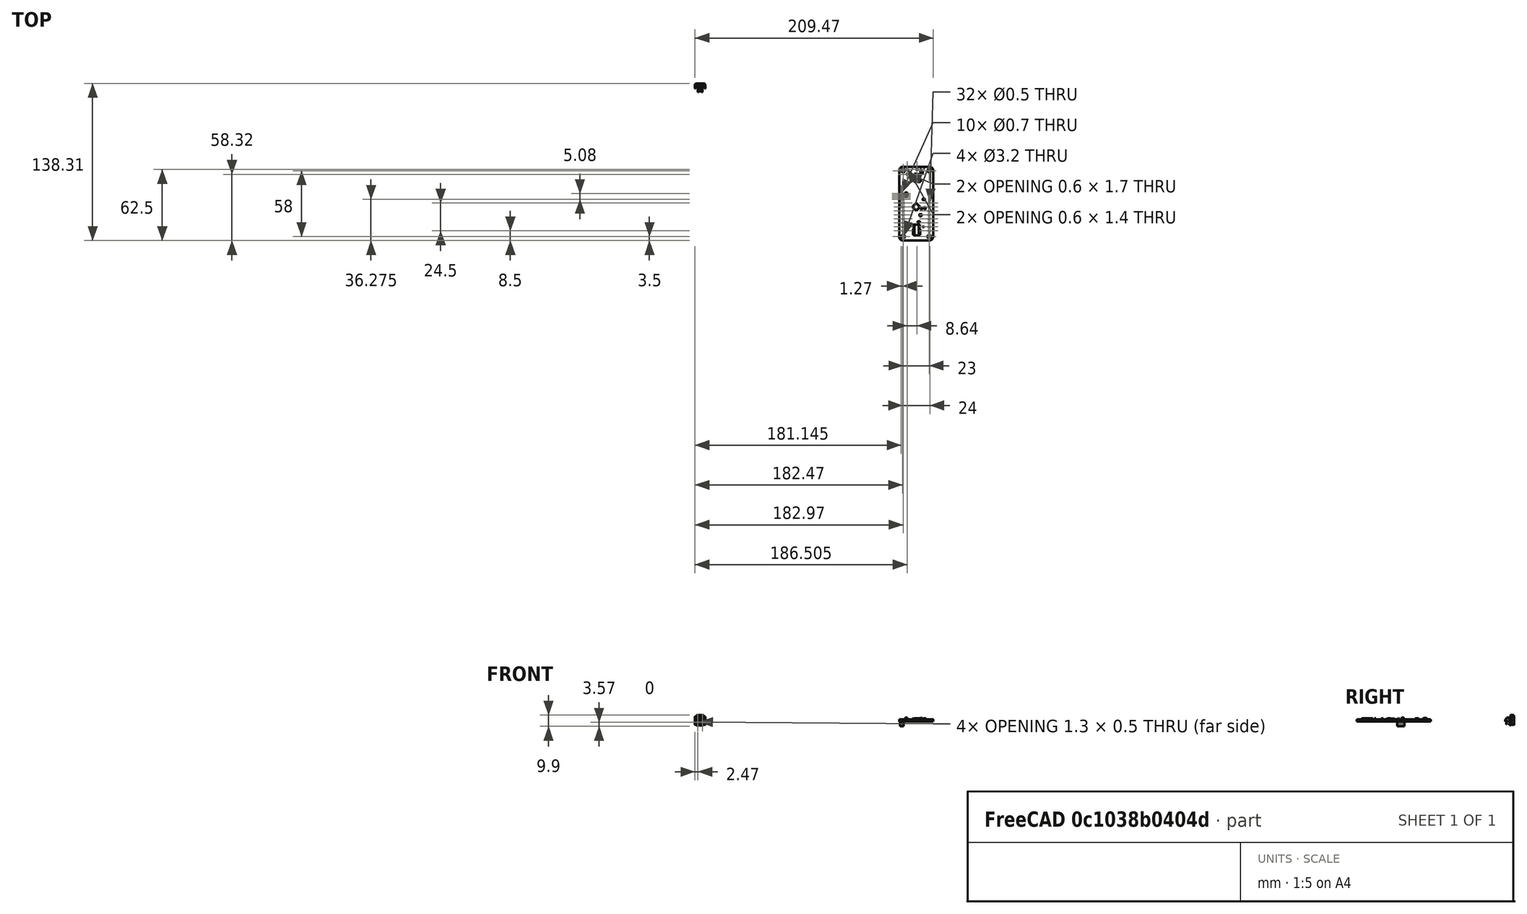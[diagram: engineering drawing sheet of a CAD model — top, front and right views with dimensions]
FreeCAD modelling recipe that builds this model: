
FCSTD DOCUMENT  (FreeCAD 0.21R33771 (Git))
Label: fc_r3
License: All rights reserved
LicenseURL: http://en.wikipedia.org/wiki/All_rights_reserved
objects: Part::Feature×103, App::Link×54, App::Part×14, PartDesign::CoordinateSystem×1, Sketcher::SketchObject×1
note: 105 computed .brp shape members not serialized (recipe doc carries the construction recipe); baked Part::Feature solids carry a one-line shape summary decoded from their .brp

FEATURE [PartDesign::CoordinateSystem] Local_CS_fc8e
  AttacherType = Attacher::AttachEngine3D
  MapMode = 2
  Support = -> [X_Axis001]
FEATURE [Part::Feature] Pcb_fc8e
  shape: bbox 30 x 65 x 1.6 mm, 85 faces (baked)
FEATURE [Sketcher::SketchObject] PCB_Sketch_fc8e
  FullyConstrained = false
  sketch-geometry (9):
    g0: LineSegment StartX=205 StartY=-73.5 StartZ=0 EndX=205 EndY=-131.5 EndZ=0
    g1: LineSegment StartX=178.5 StartY=-135 StartZ=0 EndX=201.5 EndY=-135 EndZ=0
    g2: LineSegment StartX=175 StartY=-73.5 StartZ=0 EndX=175 EndY=-131.5 EndZ=0
    g3: LineSegment StartX=178.5 StartY=-70 StartZ=0 EndX=197 EndY=-70 EndZ=0
    g4: LineSegment StartX=197 StartY=-70 StartZ=0 EndX=201.5 EndY=-70 EndZ=0
    g5: ArcOfCircle CenterX=178.5 CenterY=-131.5 CenterZ=0 NormalX=0 NormalY=0 NormalZ=-1 AngleXU=-1.5708 Radius=3.5 StartAngle=0 EndAngle=1.5708
    g6: ArcOfCircle CenterX=201.5 CenterY=-131.5 CenterZ=0 NormalX=0 NormalY=0 NormalZ=-1 AngleXU=3.14159 Radius=3.5 StartAngle=0 EndAngle=1.5708
    g7: ArcOfCircle CenterX=178.5 CenterY=-73.5 CenterZ=0 NormalX=0 NormalY=0 NormalZ=-1 AngleXU=-2.59331e-07 Radius=3.5 StartAngle=0 EndAngle=1.5708
    g8: ArcOfCircle CenterX=201.5 CenterY=-73.5 CenterZ=0 NormalX=0 NormalY=0 NormalZ=-1 AngleXU=1.5708 Radius=3.5 StartAngle=0 EndAngle=1.5708
  constraints (9):
    c: Coincident(g2,g5)
    c: Coincident(g2,g7)
    c: Coincident(g1,g5)
    c: Coincident(g3,g7)
    c: Coincident(g3,g4)
    c: Coincident(g1,g6)
    c: Coincident(g4,g8)
    c: Coincident(g0,g6)
    c: Coincident(g0,g8)
FEATURE [App::Part] Board_Geoms_fc8e
  Group = -> [Pcb_fc8e,PCB_Sketch_fc8e]
  Origin = -> Origin
FEATURE [Part::Feature] Part__Feature  label="SOLID"
  shape: bbox 4.25 x 5.5 x 5.806 mm, 112 faces (baked)
FEATURE [App::Part] _30480210  label="J15_530480210_eba29879c98""
  Group = -> [Part__Feature]
  Origin = -> Origin008
  Placement = pos=(178.75,-116,3) rot=(1,0,0;1.5708rad)
FEATURE [Part::Feature] Shape  label="AP2112K-3.3V2_SOT_23_5_dac772f8d32""
  Placement = pos=(194.5,-75,0) rot=(0,0,1;3.14159rad)
  shape: bbox 2.8 x 2.9 x 1.55 mm, 109 faces (baked)
FEATURE [Part::Feature] Shape001  label="R31_R_0402_1005Metric_05aedb9767e""
  Placement = pos=(196.225,-123.071,0) rot=(0,0,1;3.14159rad)
  shape: bbox 1 x 0.5 x 0.35 mm, 26 faces (baked)
FEATURE [App::Link] J15_530480210_eba29879c98__ln_  label="J12_530480210_0c2ba19a673""
  LinkPlacement = pos=(178.75,-105.5,3) rot=(1,0,0;1.5708rad)
  LinkedObject = -> _30480210
  Placement = pos=(178.75,-105.5,3) rot=(1,0,0;1.5708rad)
FEATURE [App::Link] J15_530480210_eba29879c98__ln_001  label="J23_530480210_43af08e91fe""
  LinkPlacement = pos=(201.25,-112.5,3) rot=(0,0.707107,0.707107;3.14159rad)
  LinkedObject = -> _30480210
  Placement = pos=(201.25,-112.5,3) rot=(0,0.707107,0.707107;3.14159rad)
FEATURE [App::Link] R31_R_0402_1005Metric_05aedb9767e__ln_  label="R3_R_0402_1005Metric_8d72cd1c525""
  LinkPlacement = pos=(196.4,-111.45,0) rot=(0,0,1;3.14159rad)
  LinkedObject = -> Shape001
  Placement = pos=(196.4,-111.45,0) rot=(0,0,1;3.14159rad)
FEATURE [App::Link] R31_R_0402_1005Metric_05aedb9767e__ln_001  label="R25_R_0402_1005Metric_978085bccb1""
  LinkPlacement = pos=(196.128,-132.5,0) rot=(0,0,1;3.14159rad)
  LinkedObject = -> Shape001
  Placement = pos=(196.128,-132.5,0) rot=(0,0,1;3.14159rad)
FEATURE [Part::Feature] Shape002  label="R17_R_0805_2012Metric_b5a45a613a7""
  Placement = pos=(196.6,-98.8,0) rot=(0,0,1;0rad)
  shape: bbox 2 x 1.2 x 0.45 mm, 26 faces (baked)
FEATURE [App::Link] J15_530480210_eba29879c98__ln_002  label="J14_530480210_c20acc79bf5""
  LinkPlacement = pos=(178.75,-112.5,3) rot=(1,0,0;1.5708rad)
  LinkedObject = -> _30480210
  Placement = pos=(178.75,-112.5,3) rot=(1,0,0;1.5708rad)
FEATURE [Part::Feature] Shape003  label="C7_C_0805_2012Metric_171301cf5fe""
  Placement = pos=(197.6,-106.6,0) rot=(0,0,1;1.5708rad)
  shape: bbox 1.25 x 2 x 1.25 mm, 28 faces (baked)
FEATURE [App::Link] R31_R_0402_1005Metric_05aedb9767e__ln_002  label="R28_R_0402_1005Metric_2c74dacb2f0""
  LinkPlacement = pos=(196.225,-127.786,0) rot=(0,0,1;3.14159rad)
  LinkedObject = -> Shape001
  Placement = pos=(196.225,-127.786,0) rot=(0,0,1;3.14159rad)
FEATURE [Part::Feature] Shape004  label="Y2_MicroCrystal_CC8V_T1A_efc3ded5715""
  Placement = pos=(194.9,-106.9,0) rot=(0,0,1;3.92699rad)
  shape: bbox 2.249 x 2.249 x 0.66 mm, 28 faces (baked)
FEATURE [App::Link] R31_R_0402_1005Metric_05aedb9767e__ln_003  label="R9_R_0402_1005Metric_35c67acb1dd""
  LinkPlacement = pos=(184.225,-121.5,0) rot=(0,0,1;0rad)
  LinkedObject = -> Shape001
  Placement = pos=(184.225,-121.5,0) rot=(0,0,1;0rad)
FEATURE [App::Link] J15_530480210_eba29879c98__ln_003  label="J18_530480210_ea0dcacd6fe""
  LinkPlacement = pos=(178.75,-126.5,3) rot=(1,0,0;1.5708rad)
  LinkedObject = -> _30480210
  Placement = pos=(178.75,-126.5,3) rot=(1,0,0;1.5708rad)
FEATURE [App::Link] R31_R_0402_1005Metric_05aedb9767e__ln_004  label="R23_R_0402_1005Metric_96d6f038491""
  LinkPlacement = pos=(184.225,-130.929,0) rot=(0,0,1;0rad)
  LinkedObject = -> Shape001
  Placement = pos=(184.225,-130.929,0) rot=(0,0,1;0rad)
FEATURE [App::Link] Y2_MicroCrystal_CC8V_T1A_efc3ded5715__ln_  label="Y1_MicroCrystal_CC8V_T1A_dfa087bb6c1""
  LinkPlacement = pos=(183.8,-109.6,0) rot=(0,0,1;3.14159rad)
  LinkedObject = -> Shape004
  Placement = pos=(183.8,-109.6,0) rot=(0,0,1;3.14159rad)
FEATURE [App::Link] R31_R_0402_1005Metric_05aedb9767e__ln_005  label="R20_R_0402_1005Metric_43ccce8d641""
  LinkPlacement = pos=(184.225,-126.214,0) rot=(0,0,1;0rad)
  LinkedObject = -> Shape001
  Placement = pos=(184.225,-126.214,0) rot=(0,0,1;0rad)
FEATURE [App::Link] R17_R_0805_2012Metric_b5a45a613a7__ln_  label="R1_R_0805_2012Metric_1946942f991""
  LinkPlacement = pos=(182.5,-81.2,0) rot=(0,0,1;1.5708rad)
  LinkedObject = -> Shape002
  Placement = pos=(182.5,-81.2,0) rot=(0,0,1;1.5708rad)
FEATURE [App::Link] C7_C_0805_2012Metric_171301cf5fe__ln_  label="C1_C_0805_2012Metric_849ba8927e4""
  LinkPlacement = pos=(183.8,-111.6,0) rot=(0,0,1;0rad)
  LinkedObject = -> Shape003
  Placement = pos=(183.8,-111.6,0) rot=(0,0,1;0rad)
FEATURE [App::Link] C7_C_0805_2012Metric_171301cf5fe__ln_001  label="C5_C_0805_2012Metric_febcc4c9503""
  LinkPlacement = pos=(183.7,-103.4,0) rot=(0,0,1;3.14159rad)
  LinkedObject = -> Shape003
  Placement = pos=(183.7,-103.4,0) rot=(0,0,1;3.14159rad)
FEATURE [App::Link] R31_R_0402_1005Metric_05aedb9767e__ln_006  label="R21_R_0402_1005Metric_75ba3e67f3f""
  LinkPlacement = pos=(184.225,-127.786,0) rot=(0,0,1;0rad)
  LinkedObject = -> Shape001
  Placement = pos=(184.225,-127.786,0) rot=(0,0,1;0rad)
FEATURE [App::Link] J15_530480210_eba29879c98__ln_004  label="J25_530480210_b44d54db2ce""
  LinkPlacement = pos=(201.25,-105.5,3) rot=(0,0.707107,0.707107;3.14159rad)
  LinkedObject = -> _30480210
  Placement = pos=(201.25,-105.5,3) rot=(0,0.707107,0.707107;3.14159rad)
FEATURE [App::Link] R17_R_0805_2012Metric_b5a45a613a7__ln_001  label="R5_R_0805_2012Metric_eb4e9e37ec6""
  LinkPlacement = pos=(196.225,-118.5,0) rot=(0,0,-1;1.5708rad)
  LinkedObject = -> Shape002
  Placement = pos=(196.225,-118.5,0) rot=(0,0,-1;1.5708rad)
FEATURE [Part::Feature] Part__Feature001  label="USB4105GFA_USB4105GFA"
  Placement = pos=(0,3e-16,-1.255) rot=(0,0,1;0rad)
  shape: bbox 0.25 x 0.05 x 2.38 mm, 6 faces (baked)
FEATURE [Part::Feature] Part__Feature002  label="USB4105GFA_USB4105GFA001"
  Placement = pos=(0,3e-16,-1.255) rot=(0,0,1;0rad)
  shape: bbox 0.25 x 0.05 x 2.38 mm, 6 faces (baked)
FEATURE [Part::Feature] Part__Feature003  label="USB4105GFA_USB4105GFA002"
  Placement = pos=(0,3e-16,-1.255) rot=(0,0,1;0rad)
  shape: bbox 0.25 x 0.05 x 1.88 mm, 6 faces (baked)
FEATURE [Part::Feature] Part__Feature004  label="USB4105GFA_USB4105GFA003"
  Placement = pos=(0,3e-16,-1.255) rot=(0,0,1;0rad)
  shape: bbox 0.25 x 0.05 x 1.88 mm, 6 faces (baked)
FEATURE [Part::Feature] Part__Feature005  label="USB4105GFA_USB4105GFA004"
  Placement = pos=(0,3e-16,-1.255) rot=(0,0,1;0rad)
  shape: bbox 0.25 x 0.05 x 1.88 mm, 6 faces (baked)
FEATURE [Part::Feature] Part__Feature006  label="USB4105GFA_USB4105GFA005"
  Placement = pos=(0,3e-16,-1.255) rot=(0,0,1;0rad)
  shape: bbox 0.25 x 0.05 x 1.88 mm, 6 faces (baked)
FEATURE [Part::Feature] Part__Feature007  label="USB4105GFA_USB4105GFA006"
  Placement = pos=(0,3e-16,-1.255) rot=(0,0,1;0rad)
  shape: bbox 0.25 x 0.05 x 1.88 mm, 6 faces (baked)
FEATURE [Part::Feature] Part__Feature008  label="USB4105GFA_USB4105GFA007"
  Placement = pos=(0,3e-16,-1.255) rot=(0,0,1;0rad)
  shape: bbox 0.25 x 0.05 x 1.88 mm, 6 faces (baked)
FEATURE [Part::Feature] Part__Feature009  label="USB4105GFA_USB4105GFA008"
  Placement = pos=(0,3e-16,-1.255) rot=(0,0,1;0rad)
  shape: bbox 0.25 x 0.05 x 1.88 mm, 6 faces (baked)
FEATURE [Part::Feature] Part__Feature010  label="USB4105GFA_USB4105GFA009"
  Placement = pos=(0,3e-16,-1.255) rot=(0,0,1;0rad)
  shape: bbox 0.25 x 0.05 x 1.88 mm, 6 faces (baked)
FEATURE [Part::Feature] Part__Feature011  label="USB4105GFA_USB4105GFA010"
  Placement = pos=(0,3e-16,-1.255) rot=(0,0,1;0rad)
  shape: bbox 0.25 x 0.05 x 2.38 mm, 6 faces (baked)
FEATURE [Part::Feature] Part__Feature012  label="USB4105GFA_USB4105GFA011"
  Placement = pos=(0,3e-16,-1.255) rot=(0,0,1;0rad)
  shape: bbox 0.25 x 0.05 x 2.38 mm, 6 faces (baked)
FEATURE [Part::Feature] Part__Feature013  label="USB4105GFA_USB4105GFA012"
  Placement = pos=(0,3e-16,-1.255) rot=(0,0,1;0rad)
  shape: bbox 0.25 x 0.05 x 2.38 mm, 6 faces (baked)
FEATURE [Part::Feature] Part__Feature014  label="USB4105GFA_USB4105GFA013"
  Placement = pos=(0,3e-16,-1.255) rot=(0,0,1;0rad)
  shape: bbox 0.25 x 0.05 x 1.88 mm, 6 faces (baked)
FEATURE [Part::Feature] Part__Feature015  label="USB4105GFA_USB4105GFA014"
  Placement = pos=(0,3e-16,-1.255) rot=(0,0,1;0rad)
  shape: bbox 0.25 x 0.05 x 1.88 mm, 6 faces (baked)
FEATURE [Part::Feature] Part__Feature016  label="USB4105GFA_USB4105GFA015"
  Placement = pos=(0,3e-16,-1.255) rot=(0,0,1;0rad)
  shape: bbox 0.25 x 0.05 x 2.38 mm, 6 faces (baked)
FEATURE [Part::Feature] Part__Feature017  label="USB4105GFA_USB4105GFA016"
  Placement = pos=(0,3e-16,-1.255) rot=(0,0,1;0rad)
  shape: bbox 0.25 x 0.05 x 1.88 mm, 6 faces (baked)
FEATURE [Part::Feature] Part__Feature018  label="USB4105GFA_USB4105GFA017"
  Placement = pos=(0,3e-16,-1.255) rot=(0,0,1;0rad)
  shape: bbox 0.25 x 0.05 x 1.88 mm, 6 faces (baked)
FEATURE [Part::Feature] Part__Feature019  label="USB4105GFA_USB4105GFA018"
  Placement = pos=(0,3e-16,-1.255) rot=(0,0,1;0rad)
  shape: bbox 0.25 x 0.05 x 1.88 mm, 6 faces (baked)
FEATURE [Part::Feature] Part__Feature020  label="USB4105GFA_USB4105GFA019"
  Placement = pos=(0,3e-16,-1.255) rot=(0,0,1;0rad)
  shape: bbox 0.25 x 0.05 x 1.88 mm, 6 faces (baked)
FEATURE [Part::Feature] Part__Feature021  label="USB4105GFA_USB4105GFA020"
  Placement = pos=(0,3e-16,-1.255) rot=(0,0,1;0rad)
  shape: bbox 0.25 x 0.05 x 2.38 mm, 6 faces (baked)
FEATURE [Part::Feature] Part__Feature022  label="USB4105GFA_USB4105GFA021"
  Placement = pos=(0,3e-16,-1.255) rot=(0,0,1;0rad)
  shape: bbox 0.25 x 0.05 x 1.88 mm, 6 faces (baked)
FEATURE [Part::Feature] Part__Feature023  label="USB4105GFA_USB4105GFA022"
  Placement = pos=(0,3e-16,-1.255) rot=(0,0,1;0rad)
  shape: bbox 0.25 x 0.05 x 1.88 mm, 6 faces (baked)
FEATURE [Part::Feature] Part__Feature024  label="USB4105GFA_USB4105GFA023"
  Placement = pos=(0,3e-16,-1.255) rot=(0,0,1;0rad)
  shape: bbox 0.25 x 0.05 x 2.38 mm, 6 faces (baked)
FEATURE [Part::Feature] Part__Feature025  label="USB4105GFA_USB4105GFA024"
  Placement = pos=(0,3e-16,-1.255) rot=(0,0,1;0rad)
  shape: bbox 0.35 x 0.1 x 1.82 mm, 9 faces (baked)
FEATURE [Part::Feature] Part__Feature026  label="USB4105GFA_USB4105GFA025"
  Placement = pos=(0,3e-16,-1.255) rot=(0,0,1;0rad)
  shape: bbox 0.35 x 0.1 x 1.82 mm, 9 faces (baked)
FEATURE [Part::Feature] Part__Feature027  label="USB4105GFA_USB4105GFA026"
  Placement = pos=(0,3e-16,-1.255) rot=(0,0,1;0rad)
  shape: bbox 0.2 x 0.32 x 0.725 mm, 10 faces (baked)
FEATURE [Part::Feature] Part__Feature028  label="USB4105GFA_USB4105GFA027"
  Placement = pos=(0,3e-16,-1.255) rot=(0,0,1;0rad)
  shape: bbox 0.2 x 0.32 x 0.725 mm, 10 faces (baked)
FEATURE [Part::Feature] Part__Feature029  label="USB4105GFA_USB4105GFA028"
  Placement = pos=(0,3e-16,-1.255) rot=(0,0,1;0rad)
  shape: bbox 0.2 x 0.32 x 0.725 mm, 10 faces (baked)
FEATURE [Part::Feature] Part__Feature030  label="USB4105GFA_USB4105GFA029"
  Placement = pos=(0,3e-16,-1.255) rot=(0,0,1;0rad)
  shape: bbox 0.2 x 0.32 x 0.725 mm, 10 faces (baked)
FEATURE [Part::Feature] Part__Feature031  label="USB4105GFA_USB4105GFA030"
  Placement = pos=(0,3e-16,-1.255) rot=(0,0,1;0rad)
  shape: bbox 0.2 x 0.32 x 0.725 mm, 10 faces (baked)
FEATURE [Part::Feature] Part__Feature032  label="USB4105GFA_USB4105GFA031"
  Placement = pos=(0,3e-16,-1.255) rot=(0,0,1;0rad)
  shape: bbox 0.2 x 0.32 x 0.725 mm, 10 faces (baked)
FEATURE [Part::Feature] Part__Feature033  label="USB4105GFA_USB4105GFA032"
  Placement = pos=(0,3e-16,-1.255) rot=(0,0,1;0rad)
  shape: bbox 0.2 x 0.32 x 0.725 mm, 10 faces (baked)
FEATURE [Part::Feature] Part__Feature034  label="USB4105GFA_USB4105GFA033"
  Placement = pos=(0,3e-16,-1.255) rot=(0,0,1;0rad)
  shape: bbox 0.2 x 0.32 x 0.725 mm, 10 faces (baked)
FEATURE [Part::Feature] Part__Feature035  label="USB4105GFA_USB4105GFA034"
  Placement = pos=(0,3e-16,-1.255) rot=(0,0,1;0rad)
  shape: bbox 0.2 x 0.32 x 0.725 mm, 10 faces (baked)
FEATURE [Part::Feature] Part__Feature036  label="USB4105GFA_USB4105GFA035"
  Placement = pos=(0,3e-16,-1.255) rot=(0,0,1;0rad)
  shape: bbox 0.2 x 0.32 x 0.725 mm, 10 faces (baked)
FEATURE [Part::Feature] Part__Feature037  label="USB4105GFA_USB4105GFA036"
  Placement = pos=(0,3e-16,-1.255) rot=(0,0,1;0rad)
  shape: bbox 0.2 x 0.32 x 0.725 mm, 10 faces (baked)
FEATURE [Part::Feature] Part__Feature038  label="USB4105GFA_USB4105GFA037"
  Placement = pos=(0,3e-16,-1.255) rot=(0,0,1;0rad)
  shape: bbox 0.2 x 0.32 x 0.725 mm, 10 faces (baked)
FEATURE [Part::Feature] Part__Feature039  label="USB4105GFA_USB4105GFA038"
  Placement = pos=(0,3e-16,-1.255) rot=(0,0,1;0rad)
  shape: bbox 0.2 x 0.32 x 0.725 mm, 10 faces (baked)
FEATURE [Part::Feature] Part__Feature040  label="USB4105GFA_USB4105GFA039"
  Placement = pos=(0,3e-16,-1.255) rot=(0,0,1;0rad)
  shape: bbox 0.2 x 0.32 x 0.725 mm, 10 faces (baked)
FEATURE [Part::Feature] Part__Feature041  label="USB4105GFA_USB4105GFA040"
  Placement = pos=(0,3e-16,-1.255) rot=(0,0,1;0rad)
  shape: bbox 0.2 x 0.32 x 0.725 mm, 10 faces (baked)
FEATURE [Part::Feature] Part__Feature042  label="USB4105GFA_USB4105GFA041"
  Placement = pos=(0,3e-16,-1.255) rot=(0,0,1;0rad)
  shape: bbox 0.2 x 0.32 x 0.725 mm, 10 faces (baked)
FEATURE [Part::Feature] Part__Feature043  label="USB4105GFA_USB4105GFA042"
  Placement = pos=(0,3e-16,-1.255) rot=(0,0,1;0rad)
  shape: bbox 8.94 x 4.41 x 7.33 mm, 421 faces (baked)
FEATURE [Part::Feature] Part__Feature044  label="USB4105GFA_USB4105GFA043"
  Placement = pos=(0,3e-16,-1.255) rot=(0,0,1;0rad)
  shape: bbox 8.89 x 3.61 x 6.57 mm, 162 faces (baked)
FEATURE [App::Part] USB4105GFA_USB4105GFA  label="USB4105GFA_USB4105GFA044"
  Group = -> [Part__Feature001,Part__Feature002,Part__Feature003,Part__Feature004,Part__Feature005,Part__Feature006,Part__Feature007,Part__Feature008,Part__Feature009,Part__Feature010,Part__Feature011,Part__Feature012,Part__Feature013,Part__Feature014,Part__Feature015,Part__Feature016,Part__Feature017,Part__Feature018,Part__Feature019,Part__Feature020,Part__Feature021,Part__Feature022,Part__Feature023,+21 more]
  Origin = -> Origin009
FEATURE [App::Part] USB4105GFA  label="J1_USB4105GFA_8c9771e9b48""
  Group = -> [USB4105GFA_USB4105GFA]
  Origin = -> Origin010
  Placement = pos=(186.355,-72.5,0) rot=(0,0.707107,0.707107;3.14159rad)
FEATURE [App::Link] J15_530480210_eba29879c98__ln_005  label="J26_530480210_0dc223683e1""
  LinkPlacement = pos=(201.25,-102,3) rot=(0,0.707107,0.707107;3.14159rad)
  LinkedObject = -> _30480210
  Placement = pos=(201.25,-102,3) rot=(0,0.707107,0.707107;3.14159rad)
FEATURE [App::Link] R17_R_0805_2012Metric_b5a45a613a7__ln_002  label="R2_R_0805_2012Metric_a13dcf4894d""
  LinkPlacement = pos=(184.225,-118.5,0) rot=(0,0,-1;1.5708rad)
  LinkedObject = -> Shape002
  Placement = pos=(184.225,-118.5,0) rot=(0,0,-1;1.5708rad)
FEATURE [App::Link] R31_R_0402_1005Metric_05aedb9767e__ln_007  label="R32_R_0402_1005Metric_2e0dea6faa5""
  LinkPlacement = pos=(196.225,-121.5,0) rot=(0,0,1;3.14159rad)
  LinkedObject = -> Shape001
  Placement = pos=(196.225,-121.5,0) rot=(0,0,1;3.14159rad)
FEATURE [App::Link] J15_530480210_eba29879c98__ln_006  label="J16_530480210_f79377288be""
  LinkPlacement = pos=(178.75,-119.5,3) rot=(1,0,0;1.5708rad)
  LinkedObject = -> _30480210
  Placement = pos=(178.75,-119.5,3) rot=(1,0,0;1.5708rad)
FEATURE [Part::Feature] Part__Feature045  label="APHB1608LZGKSURKC_APHB1608LZGKSURKC"
  Placement = pos=(0,0,0) rot=(0,1,0;1.5708rad)
  shape: bbox 0.4 x 0.15 x 0.3 mm, 7 faces (baked)
FEATURE [Part::Feature] Part__Feature046  label="APHB1608LZGKSURKC_APHB1608LZGKSURKC001"
  Placement = pos=(0,0,0) rot=(0,1,0;1.5708rad)
  shape: bbox 0.4 x 0.15 x 0.3 mm, 7 faces (baked)
FEATURE [Part::Feature] Part__Feature047  label="APHB1608LZGKSURKC_APHB1608LZGKSURKC002"
  Placement = pos=(0,0,0) rot=(0,1,0;1.5708rad)
  shape: bbox 0.4 x 0.15 x 0.3 mm, 7 faces (baked)
FEATURE [Part::Feature] Part__Feature048  label="APHB1608LZGKSURKC_APHB1608LZGKSURKC003"
  Placement = pos=(0,0,0) rot=(0,1,0;1.5708rad)
  shape: bbox 0.4 x 0.15 x 0.3 mm, 7 faces (baked)
FEATURE [Part::Feature] Part__Feature049  label="APHB1608LZGKSURKC_APHB1608LZGKSURKC004"
  Placement = pos=(0,0,0) rot=(0,1,0;1.5708rad)
  shape: bbox 0.15 x 0.15 x 0.15 mm, 5 faces (baked)
FEATURE [Part::Feature] Part__Feature050  label="APHB1608LZGKSURKC_APHB1608LZGKSURKC005"
  Placement = pos=(0,0,0) rot=(0,1,0;1.5708rad)
  shape: bbox 0.15 x 0.15 x 0.15 mm, 5 faces (baked)
FEATURE [Part::Feature] Part__Feature051  label="APHB1608LZGKSURKC_APHB1608LZGKSURKC006"
  Placement = pos=(0,0,0) rot=(0,1,0;1.5708rad)
  shape: bbox 0.15 x 0.15 x 0.15 mm, 5 faces (baked)
FEATURE [Part::Feature] Part__Feature052  label="APHB1608LZGKSURKC_APHB1608LZGKSURKC007"
  Placement = pos=(0,0,0) rot=(0,1,0;1.5708rad)
  shape: bbox 0.15 x 0.15 x 0.15 mm, 5 faces (baked)
FEATURE [Part::Feature] Part__Feature053  label="APHB1608LZGKSURKC_APHB1608LZGKSURKC008"
  Placement = pos=(0,0,0) rot=(0,1,0;1.5708rad)
  shape: bbox 1.6 x 0.35 x 0.8 mm, 6 faces (baked)
FEATURE [Part::Feature] Part__Feature054  label="APHB1608LZGKSURKC_APHB1608LZGKSURKC009"
  Placement = pos=(0,0,0) rot=(0,1,0;1.5708rad)
  shape: bbox 1.6 x 0.15 x 0.8 mm, 23 faces (baked)
FEATURE [Part::Feature] Part__Feature055  label="APHB1608LZGKSURKC_APHB1608LZGKSURKC010"
  Placement = pos=(0,0,0) rot=(0,1,0;1.5708rad)
  shape: bbox 0.4 x 0.1 x 0.796 mm, 10 faces (baked)
FEATURE [App::Part] APHB1608LZGKSURKC_APHB1608LZGKSURKC  label="APHB1608LZGKSURKC_APHB1608LZGKSURKC011"
  Group = -> [Part__Feature045,Part__Feature046,Part__Feature047,Part__Feature048,Part__Feature049,Part__Feature050,Part__Feature051,Part__Feature052,Part__Feature053,Part__Feature054,Part__Feature055]
  Origin = -> Origin011
FEATURE [App::Part] APHB1608LZGKSURKC  label="D6_APHB1608LZGKSURKC_2d79be0c02d""
  Group = -> [APHB1608LZGKSURKC_APHB1608LZGKSURKC]
  Origin = -> Origin012
  Placement = pos=(196.4,-112.8,0) rot=(0,0.707107,0.707107;3.14159rad)
FEATURE [App::Link] C7_C_0805_2012Metric_171301cf5fe__ln_002  label="C6_C_0805_2012Metric_464f59ece5b""
  LinkPlacement = pos=(183.7,-101.3,0) rot=(0,0,1;0rad)
  LinkedObject = -> Shape003
  Placement = pos=(183.7,-101.3,0) rot=(0,0,1;0rad)
FEATURE [App::Link] R31_R_0402_1005Metric_05aedb9767e__ln_008  label="R29_R_0402_1005Metric_32d439146da""
  LinkPlacement = pos=(196.225,-126.214,0) rot=(0,0,1;3.14159rad)
  LinkedObject = -> Shape001
  Placement = pos=(196.225,-126.214,0) rot=(0,0,1;3.14159rad)
FEATURE [Part::Feature] Shape005  label="RESET1_B3U_1000P[]_5c0dfc48375""
  Placement = pos=(181.2,-94.6,0) rot=(0.57735,-0.57735,-0.57735;2.0944rad)
  shape: bbox 2.5 x 4 x 1.6 mm, 77 faces (baked)
FEATURE [App::Link] R17_R_0805_2012Metric_b5a45a613a7__ln_003  label="R15_R_0805_2012Metric_2045c3087e7""
  LinkPlacement = pos=(184.5,-81.2,0) rot=(0,0,-1;1.5708rad)
  LinkedObject = -> Shape002
  Placement = pos=(184.5,-81.2,0) rot=(0,0,-1;1.5708rad)
FEATURE [Part::Feature] Shape006  label="U3_QFN_32_1EP_5x5mm_P05mm_EP33x33mm_5e3dba8b24a""
  Placement = pos=(190,-105.3,0) rot=(0,0,1;0.785398rad)
  shape: bbox 7.036 x 7.036 x 0.875 mm, 206 faces (baked)
FEATURE [App::Link] R31_R_0402_1005Metric_05aedb9767e__ln_009  label="R27_R_0402_1005Metric_b2657f9fb6a""
  LinkPlacement = pos=(196.225,-129.357,0) rot=(0,0,1;3.14159rad)
  LinkedObject = -> Shape001
  Placement = pos=(196.225,-129.357,0) rot=(0,0,1;3.14159rad)
FEATURE [App::Link] R17_R_0805_2012Metric_b5a45a613a7__ln_004  label="R19_R_0805_2012Metric_b859e94313a""
  LinkPlacement = pos=(196.6,-96.5,0) rot=(0,0,1;3.14159rad)
  LinkedObject = -> Shape002
  Placement = pos=(196.6,-96.5,0) rot=(0,0,1;3.14159rad)
FEATURE [App::Link] R31_R_0402_1005Metric_05aedb9767e__ln_010  label="R26_R_0402_1005Metric_d4dea5bbcb8""
  LinkPlacement = pos=(196.128,-130.929,0) rot=(0,0,1;3.14159rad)
  LinkedObject = -> Shape001
  Placement = pos=(196.128,-130.929,0) rot=(0,0,1;3.14159rad)
FEATURE [App::Link] C7_C_0805_2012Metric_171301cf5fe__ln_003  label="C2_C_0805_2012Metric_2f69d11e048""
  LinkPlacement = pos=(183.8,-113.6,0) rot=(0,0,1;0rad)
  LinkedObject = -> Shape003
  Placement = pos=(183.8,-113.6,0) rot=(0,0,1;0rad)
FEATURE [App::Link] C7_C_0805_2012Metric_171301cf5fe__ln_004  label="C8_C_0805_2012Metric_8526150a806""
  LinkPlacement = pos=(196.6,-103.9,0) rot=(0,0,1;0rad)
  LinkedObject = -> Shape003
  Placement = pos=(196.6,-103.9,0) rot=(0,0,1;0rad)
FEATURE [Part::Feature] Shape007  label="U5_TSSOP_8_44x3mm_P065mm_c1ff1356c96""
  Placement = pos=(191,-82.1,0) rot=(0,0,1;3.14159rad)
  shape: bbox 6.4 x 3 x 1.1 mm, 156 faces (baked)
FEATURE [App::Link] J15_530480210_eba29879c98__ln_007  label="J20_530480210_a2b915e6096""
  LinkPlacement = pos=(201.25,-123,3) rot=(0,0.707107,0.707107;3.14159rad)
  LinkedObject = -> _30480210
  Placement = pos=(201.25,-123,3) rot=(0,0.707107,0.707107;3.14159rad)
FEATURE [Part::Feature] Part__Feature056  label="SM04B-SRSS-TB(LF)(SN)"
  shape: bbox 0.2 x 1.25 x 1.5 mm, 25 faces (baked)
FEATURE [Part::Feature] Part__Feature057  label="SM04B-SRSS-TB(LF)(SN)001"
  shape: bbox 0.2 x 2.46 x 3.7 mm, 20 faces (baked)
FEATURE [Part::Feature] Part__Feature058  label="SM04B-SRSS-TB(LF)(SN)002"
  shape: bbox 0.2 x 2.46 x 3.7 mm, 20 faces (baked)
FEATURE [Part::Feature] Part__Feature059  label="SM04B-SRSS-TB(LF)(SN)003"
  shape: bbox 0.2 x 2.46 x 3.7 mm, 20 faces (baked)
FEATURE [Part::Feature] Part__Feature060  label="SM04B-SRSS-TB(LF)(SN)004"
  shape: bbox 0.2 x 1.25 x 1.5 mm, 25 faces (baked)
FEATURE [Part::Feature] Part__Feature061  label="SM04B-SRSS-TB(LF)(SN)005"
  shape: bbox 0.2 x 2.46 x 3.7 mm, 20 faces (baked)
FEATURE [Part::Feature] Part__Feature062  label="SM04B-SRSS-TB(LF)(SN)006"
  shape: bbox 6 x 2.9 x 4.25 mm, 99 faces (baked)
FEATURE [App::Part] SM04B_SRSS_TB_LF__SN_  label="J10_SM04B-SRSS-TB(LF)(SN)007_7ff0f795162""
  Group = -> [Part__Feature056,Part__Feature057,Part__Feature058,Part__Feature059,Part__Feature060,Part__Feature061,Part__Feature062]
  Origin = -> Origin013
  Placement = pos=(177.925,-80.3,-0.5) rot=(0.57735,-0.57735,-0.57735;2.0944rad)
FEATURE [App::Link] C7_C_0805_2012Metric_171301cf5fe__ln_005  label="C3_C_0805_2012Metric_948c026d24f""
  LinkPlacement = pos=(198.5,-80.5,0) rot=(0,0,-1;1.5708rad)
  LinkedObject = -> Shape003
  Placement = pos=(198.5,-80.5,0) rot=(0,0,-1;1.5708rad)
FEATURE [App::Link] J10_SM04B_SRSS_TB_LF__SN_007_7ff0f795162__ln_  label="J2_SM04B-SRSS-TB(LF)(SN)007_5f22bbe0af1""
  LinkPlacement = pos=(202.1,-80.3,-0.5) rot=(0.57735,0.57735,0.57735;2.0944rad)
  LinkedObject = -> SM04B_SRSS_TB_LF__SN_
  Placement = pos=(202.1,-80.3,-0.5) rot=(0.57735,0.57735,0.57735;2.0944rad)
FEATURE [App::Link] R31_R_0402_1005Metric_05aedb9767e__ln_011  label="R10_R_0402_1005Metric_4869f4c0b29""
  LinkPlacement = pos=(184.225,-123.071,0) rot=(0,0,1;0rad)
  LinkedObject = -> Shape001
  Placement = pos=(184.225,-123.071,0) rot=(0,0,1;0rad)
FEATURE [App::Link] R17_R_0805_2012Metric_b5a45a613a7__ln_005  label="R13_R_0805_2012Metric_0160fac3375""
  LinkPlacement = pos=(196.6,-100.8,0) rot=(0,0,1;0rad)
  LinkedObject = -> Shape002
  Placement = pos=(196.6,-100.8,0) rot=(0,0,1;0rad)
FEATURE [App::Link] R31_R_0402_1005Metric_05aedb9767e__ln_012  label="R16_R_0402_1005Metric_9f33b905af8""
  LinkPlacement = pos=(196.4,-114.15,0) rot=(0,0,1;0rad)
  LinkedObject = -> Shape001
  Placement = pos=(196.4,-114.15,0) rot=(0,0,1;0rad)
FEATURE [App::Link] J15_530480210_eba29879c98__ln_008  label="J13_530480210_56933f0e703""
  LinkPlacement = pos=(178.75,-109,3) rot=(1,0,0;1.5708rad)
  LinkedObject = -> _30480210
  Placement = pos=(178.75,-109,3) rot=(1,0,0;1.5708rad)
FEATURE [Part::Feature] Shape008  label="U2_TSSOP_28_44x97mm_P065mm_7504b019951""
  Placement = pos=(190.363,-125.775,0) rot=(0,0,1;0rad)
  shape: bbox 6.4 x 9.7 x 1.1 mm, 456 faces (baked)
FEATURE [Part::Feature] Shape009  label="D2_LED_0805_2012Metric_617619232d8""
  Placement = pos=(192.27,-118.725,0) rot=(0,0,1;0rad)
  shape: bbox 2 x 1.25 x 1.1 mm, 50 faces (baked)
FEATURE [App::Link] R31_R_0402_1005Metric_05aedb9767e__ln_013  label="R18_R_0402_1005Metric_19e97eaa38b""
  LinkPlacement = pos=(184.225,-124.643,0) rot=(0,0,1;0rad)
  LinkedObject = -> Shape001
  Placement = pos=(184.225,-124.643,0) rot=(0,0,1;0rad)
FEATURE [App::Link] R17_R_0805_2012Metric_b5a45a613a7__ln_006  label="R6_R_0805_2012Metric_322051c1cd9""
  LinkPlacement = pos=(196.6,-94.5,0) rot=(0,0,1;3.14159rad)
  LinkedObject = -> Shape002
  Placement = pos=(196.6,-94.5,0) rot=(0,0,1;3.14159rad)
FEATURE [App::Link] J15_530480210_eba29879c98__ln_009  label="J19_530480210_0d22967ee7f""
  LinkPlacement = pos=(201.25,-126.5,3) rot=(0,0.707107,0.707107;3.14159rad)
  LinkedObject = -> _30480210
  Placement = pos=(201.25,-126.5,3) rot=(0,0.707107,0.707107;3.14159rad)
FEATURE [App::Link] R31_R_0402_1005Metric_05aedb9767e__ln_014  label="R22_R_0402_1005Metric_086bd447089""
  LinkPlacement = pos=(184.225,-129.357,0) rot=(0,0,1;0rad)
  LinkedObject = -> Shape001
  Placement = pos=(184.225,-129.357,0) rot=(0,0,1;0rad)
FEATURE [App::Link] R17_R_0805_2012Metric_b5a45a613a7__ln_007  label="R8_R_0805_2012Metric_1fa6d87f679""
  LinkPlacement = pos=(188.225,-118.725,0) rot=(0,0,1;3.14159rad)
  LinkedObject = -> Shape002
  Placement = pos=(188.225,-118.725,0) rot=(0,0,1;3.14159rad)
FEATURE [App::Link] R31_R_0402_1005Metric_05aedb9767e__ln_015  label="R24_R_0402_1005Metric_2800a74619b""
  LinkPlacement = pos=(184.225,-132.5,0) rot=(0,0,1;0rad)
  LinkedObject = -> Shape001
  Placement = pos=(184.225,-132.5,0) rot=(0,0,1;0rad)
FEATURE [App::Link] J10_SM04B_SRSS_TB_LF__SN_007_7ff0f795162__ln_001  label="J7_SM04B-SRSS-TB(LF)(SN)007_386b064daf5""
  LinkPlacement = pos=(177.925,-87.9,-0.5) rot=(0.57735,-0.57735,-0.57735;2.0944rad)
  LinkedObject = -> SM04B_SRSS_TB_LF__SN_
  Placement = pos=(177.925,-87.9,-0.5) rot=(0.57735,-0.57735,-0.57735;2.0944rad)
FEATURE [App::Link] J15_530480210_eba29879c98__ln_010  label="J11_530480210_72323117d84""
  LinkPlacement = pos=(178.75,-102,3) rot=(1,0,0;1.5708rad)
  LinkedObject = -> _30480210
  Placement = pos=(178.75,-102,3) rot=(1,0,0;1.5708rad)
FEATURE [App::Link] C7_C_0805_2012Metric_171301cf5fe__ln_006  label="C4_C_0805_2012Metric_3f2d9b8291f""
  LinkPlacement = pos=(196.5,-80.5,0) rot=(0,0,-1;1.5708rad)
  LinkedObject = -> Shape003
  Placement = pos=(196.5,-80.5,0) rot=(0,0,-1;1.5708rad)
FEATURE [Part::Feature] Shape010  label="U1_SOT_353_SC_70_5_e2bbc67c9be""
  Placement = pos=(193.8,-112.7,0) rot=(0,0,1;1.5708rad)
  shape: bbox 2 x 2 x 1.05 mm, 104 faces (baked)
FEATURE [Part::Feature] Part__Feature063  label="SSAJ110100"
  shape: bbox 1.2 x 0.6 x 1.935 mm, 16 faces (baked)
FEATURE [Part::Feature] Part__Feature064  label="SSAJ110101"
  shape: bbox 6.5 x 0.7 x 2.5 mm, 205 faces (baked)
FEATURE [Part::Feature] Part__Feature065  label="SSAJ110102"
  shape: bbox 0.4 x 0.35 x 0.1799 mm, 10 faces (baked)
FEATURE [Part::Feature] Part__Feature066  label="SSAJ110103"
  shape: bbox 0.4 x 0.35 x 0.1799 mm, 10 faces (baked)
FEATURE [Part::Feature] Part__Feature067  label="SSAJ110104"
  shape: bbox 0.4 x 0.35 x 0.1799 mm, 10 faces (baked)
FEATURE [Part::Feature] Part__Feature068  label="SSAJ110105"
  shape: bbox 0.275 x 0.045 x 0.05 mm, 6 faces (baked)
FEATURE [Part::Feature] Part__Feature069  label="SSAJ110106"
  shape: bbox 0.275 x 0.045 x 0.05 mm, 6 faces (baked)
FEATURE [Part::Feature] Part__Feature070  label="SSAJ110107"
  shape: bbox 0.275 x 0.045 x 0.05 mm, 6 faces (baked)
FEATURE [Part::Feature] Part__Feature071  label="SSAJ110108"
  shape: bbox 5.5 x 1.1 x 2.5 mm, 96 faces (baked)
FEATURE [Part::Feature] Part__Feature072  label="SSAJ110109"
  shape: bbox 0.9441 x 0.05 x 0.355 mm, 12 faces (baked)
FEATURE [App::Part] SSAJ110100  label="S2_SSAJ110110_94bf4a2374a""
  Group = -> [Part__Feature063,Part__Feature064,Part__Feature065,Part__Feature066,Part__Feature067,Part__Feature068,Part__Feature069,Part__Feature070,Part__Feature071,Part__Feature072]
  Origin = -> Origin014
  Placement = pos=(195.5,-70.72,0) rot=(0,0.707107,0.707107;3.14159rad)
FEATURE [App::Link] J15_530480210_eba29879c98__ln_011  label="J21_530480210_3ca28972e12""
  LinkPlacement = pos=(201.25,-119.5,3) rot=(0,0.707107,0.707107;3.14159rad)
  LinkedObject = -> _30480210
  Placement = pos=(201.25,-119.5,3) rot=(0,0.707107,0.707107;3.14159rad)
FEATURE [App::Link] J15_530480210_eba29879c98__ln_012  label="J24_530480210_d5664d251e9""
  LinkPlacement = pos=(201.25,-109,3) rot=(0,0.707107,0.707107;3.14159rad)
  LinkedObject = -> _30480210
  Placement = pos=(201.25,-109,3) rot=(0,0.707107,0.707107;3.14159rad)
FEATURE [App::Link] R17_R_0805_2012Metric_b5a45a613a7__ln_008  label="R7_R_0805_2012Metric_f3b1fd9ed19""
  LinkPlacement = pos=(202.9,-95.4,0) rot=(0,0,1;3.14159rad)
  LinkedObject = -> Shape002
  Placement = pos=(202.9,-95.4,0) rot=(0,0,1;3.14159rad)
FEATURE [App::Link] J15_530480210_eba29879c98__ln_013  label="J22_530480210_ab6988eedfa""
  LinkPlacement = pos=(201.25,-116,3) rot=(0,0.707107,0.707107;3.14159rad)
  LinkedObject = -> _30480210
  Placement = pos=(201.25,-116,3) rot=(0,0.707107,0.707107;3.14159rad)
FEATURE [App::Link] R31_R_0402_1005Metric_05aedb9767e__ln_016  label="R30_R_0402_1005Metric_b8b4026dcdc""
  LinkPlacement = pos=(196.225,-124.643,0) rot=(0,0,1;3.14159rad)
  LinkedObject = -> Shape001
  Placement = pos=(196.225,-124.643,0) rot=(0,0,1;3.14159rad)
FEATURE [App::Link] J15_530480210_eba29879c98__ln_014  label="J17_530480210_1697216bf9c""
  LinkPlacement = pos=(178.75,-123,3) rot=(1,0,0;1.5708rad)
  LinkedObject = -> _30480210
  Placement = pos=(178.75,-123,3) rot=(1,0,0;1.5708rad)
FEATURE [App::Link] R17_R_0805_2012Metric_b5a45a613a7__ln_009  label="R4_R_0805_2012Metric_03a2e8e0d08""
  LinkPlacement = pos=(189.5,-79,0) rot=(0,0,1;3.14159rad)
  LinkedObject = -> Shape002
  Placement = pos=(189.5,-79,0) rot=(0,0,1;3.14159rad)
FEATURE [App::Link] RESET1_B3U_1000P___5c0dfc48375__ln_  label="BTN1_B3U_1000P[]_c1415e18403""
  LinkPlacement = pos=(202.5,-98.2,0) rot=(0,0.707107,0.707107;3.14159rad)
  LinkedObject = -> Shape005
  Placement = pos=(202.5,-98.2,0) rot=(0,0.707107,0.707107;3.14159rad)
FEATURE [App::Part] Top_fc8e
  Group = -> [_30480210,Shape,Shape001,J15_530480210_eba29879c98__ln_,J15_530480210_eba29879c98__ln_001,R31_R_0402_1005Metric_05aedb9767e__ln_,R31_R_0402_1005Metric_05aedb9767e__ln_001,Shape002,J15_530480210_eba29879c98__ln_002,Shape003,R31_R_0402_1005Metric_05aedb9767e__ln_002,Shape004,R31_R_0402_1005Metric_05aedb9767e__ln_003,J15_530480210_eba29879c98__ln_003,R31_R_0402_1005Metric_05aedb9767e__ln_004,+54 more]
  Origin = -> Origin003
FEATURE [Part::Feature] Part__Feature073  label="Body"
  Placement = pos=(0,0,0.1) rot=(0,0,1;0rad)
  shape: bbox 4.7 x 1.7 x 0.68 mm, 6 faces (baked)
FEATURE [Part::Feature] Part__Feature074  label="Pins"
  shape: bbox 0.144 x 0.374 x 0.1 mm, 6 faces (baked)
FEATURE [Part::Feature] Part__Feature075  label="Pins001"
  shape: bbox 0.144 x 0.374 x 0.1 mm, 6 faces (baked)
FEATURE [Part::Feature] Part__Feature076  label="Pins002"
  shape: bbox 0.144 x 0.374 x 0.1 mm, 6 faces (baked)
FEATURE [Part::Feature] Part__Feature077  label="Pins003"
  shape: bbox 0.144 x 0.374 x 0.1 mm, 6 faces (baked)
FEATURE [Part::Feature] Part__Feature078  label="Pins004"
  shape: bbox 0.144 x 0.374 x 0.1 mm, 6 faces (baked)
FEATURE [Part::Feature] Part__Feature079  label="Pins005"
  shape: bbox 0.144 x 0.374 x 0.1 mm, 6 faces (baked)
FEATURE [Part::Feature] Part__Feature080  label="Pins006"
  shape: bbox 0.144 x 0.374 x 0.1 mm, 6 faces (baked)
FEATURE [Part::Feature] Part__Feature081  label="Pins007"
  shape: bbox 0.144 x 0.374 x 0.1 mm, 6 faces (baked)
FEATURE [Part::Feature] Part__Feature082  label="Pins008"
  shape: bbox 0.144 x 0.374 x 0.1 mm, 6 faces (baked)
FEATURE [Part::Feature] Part__Feature083  label="Pins009"
  shape: bbox 0.144 x 0.374 x 0.1 mm, 6 faces (baked)
FEATURE [Part::Feature] Part__Feature084  label="Pins010"
  shape: bbox 0.144 x 0.374 x 0.1 mm, 6 faces (baked)
FEATURE [Part::Feature] Part__Feature085  label="Pins011"
  shape: bbox 0.144 x 0.374 x 0.1 mm, 6 faces (baked)
FEATURE [Part::Feature] Part__Feature086  label="Pins012"
  shape: bbox 0.468 x 0.248 x 0.1 mm, 6 faces (baked)
FEATURE [Part::Feature] Part__Feature087  label="Pins013"
  shape: bbox 0.468 x 0.248 x 0.1 mm, 6 faces (baked)
FEATURE [Part::Feature] Part__Feature088  label="Pins014"
  shape: bbox 0.468 x 0.248 x 0.1 mm, 6 faces (baked)
FEATURE [Part::Feature] Part__Feature089  label="Pins015"
  shape: bbox 0.468 x 0.248 x 0.1 mm, 6 faces (baked)
FEATURE [App::Part] Pins  label="Pins016"
  Group = -> [Part__Feature074,Part__Feature075,Part__Feature076,Part__Feature077,Part__Feature078,Part__Feature079,Part__Feature080,Part__Feature081,Part__Feature082,Part__Feature083,Part__Feature084,Part__Feature085,Part__Feature086,Part__Feature087,Part__Feature088,Part__Feature089]
  Origin = -> Origin015
FEATURE [App::Part] ASSEMBLY  label="J8_ASSEMBLY_e2a3394181b""
  Group = -> [Part__Feature073,Pins]
  Origin = -> Origin016
  Placement = pos=(190,-90,-1.6) rot=(0,1,0;3.14159rad)
FEATURE [App::Link] J8_ASSEMBLY_e2a3394181b__ln_  label="J3_ASSEMBLY_42d16be3a66""
  LinkPlacement = pos=(190,-115,-1.6) rot=(1,0,0;3.14159rad)
  LinkedObject = -> ASSEMBLY
  Placement = pos=(190,-115,-1.6) rot=(1,0,0;3.14159rad)
FEATURE [Part::Feature] Shape011  label="J4_PinSocket_2x05_P127mm_Vertical_4835f2a1352""
  Placement = pos=(177.945,-98.725,-1.6) rot=(1,0,0;3.14159rad)
  shape: bbox 3.05 x 6.35 x 7 mm, 320 faces (baked)
FEATURE [App::Part] Bot_fc8e
  Group = -> [ASSEMBLY,J8_ASSEMBLY_e2a3394181b__ln_,Shape011]
  Origin = -> Origin004
FEATURE [App::Part] Step_Models_fc8e
  Group = -> [Top_fc8e,Bot_fc8e]
  Origin = -> Origin002
FEATURE [App::Part] Board_fc8e  label="LegoLight_R3"
  Group = -> [Local_CS_fc8e,Board_Geoms_fc8e,Step_Models_fc8e]
  Origin = -> Origin001
